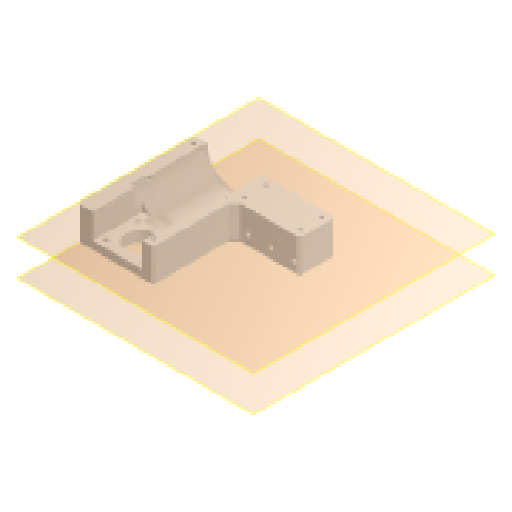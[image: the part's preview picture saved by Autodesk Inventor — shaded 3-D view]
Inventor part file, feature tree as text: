
AUTODESK INVENTOR PART (.ipt)
format: ipt  version: 2024.1 (Build 281209000, 209)  size: 306,176 bytes
history: native  units: mm
features: sketch x7, other x3, plane x2
ambient origin geometry x8: Origin, YZ Plane, XZ Plane, XY Plane, X Axis, Y Axis, Z Axis, Center Point
bodies: Volumenkörper1 (feature_tree)
feature tree (12):
  other  "MIAB_Case_v0.ipt"
  other  "Volumenkörper1::MIAB_Case_v0.ipt"
  other  "Bezeichnung1"
  sketch  "Skizze1"  dims[d0=10.0mm]
  sketch  "Skizze2"
  sketch  "Skizze3"
  sketch  "Skizze4"
  sketch  "Skizze5"
  sketch  "Skizze6"
  sketch  "Skizze7"
  plane  "Arbeitsebene1"
  plane  "Arbeitsebene2"
